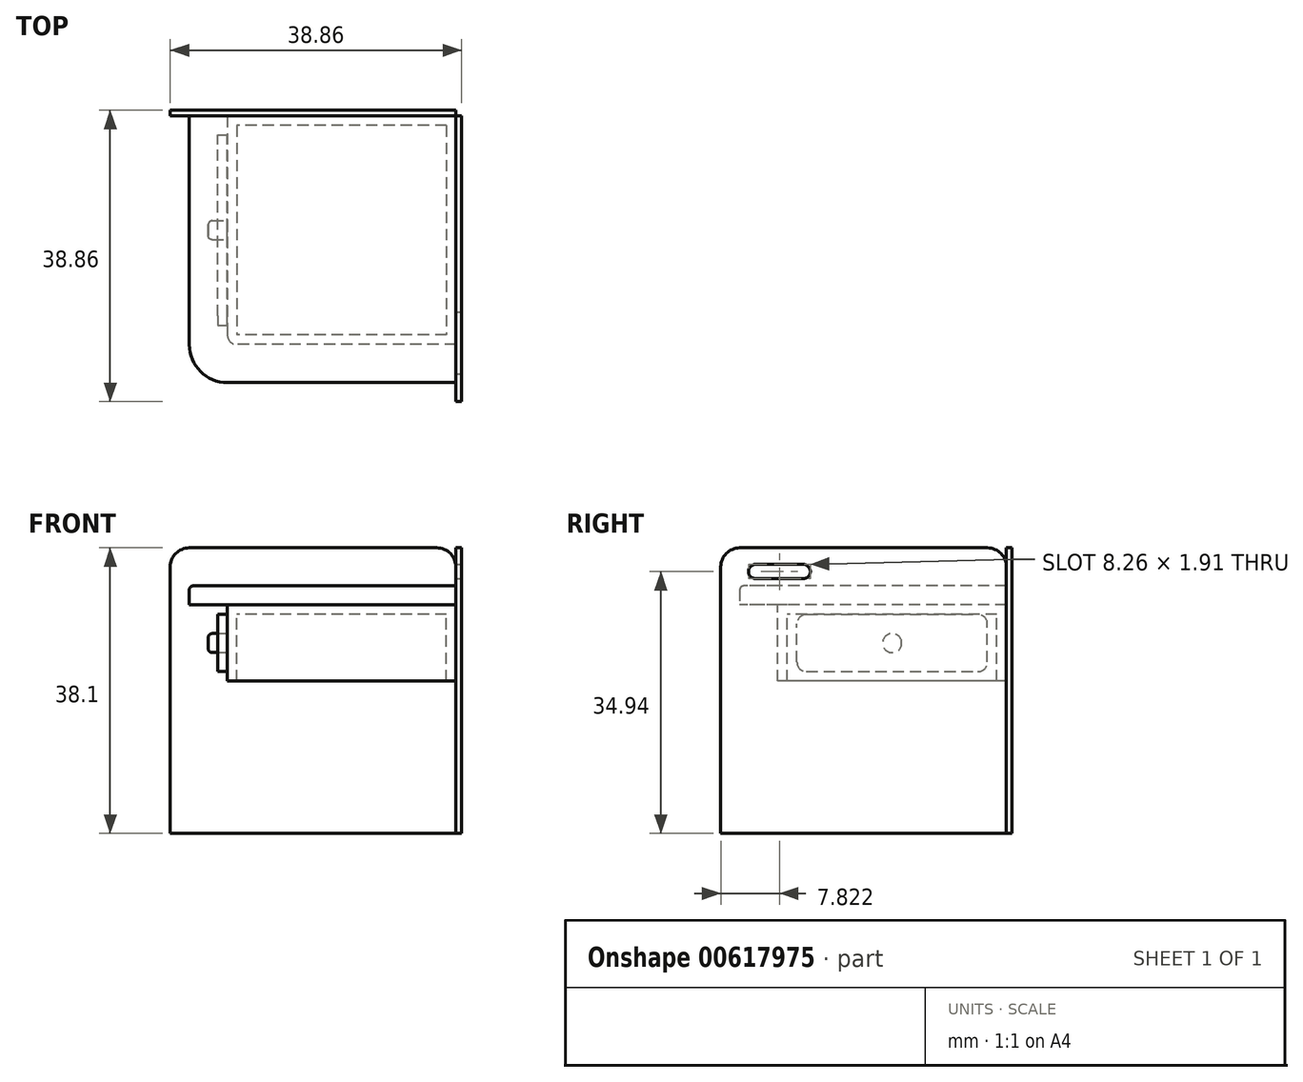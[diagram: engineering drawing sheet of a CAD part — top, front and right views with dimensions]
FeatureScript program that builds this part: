
annotation { "Feature Type Name" : "Feature", "Feature Type Description" : "" }
export const myFeature = defineFeature(function(context is Context, id is Id, definition is map)
    precondition{}
    {
        {
            var Q0;
            Q0=qCreatedBy(makeId("Right.planeOp"),FACE);
            var sketch = newSketch(context, id + "F0", { "sketchPlane" : qUnion([Q0])});
            skLineSegment(sketch, "E0.bottom", {"start": v(0, 0) * mm, "end": v(-38.1, 0) * mm});
            skLineSegment(sketch, "E0.top", {"start": v(0, 38.1) * mm, "end": v(-38.1, 38.1) * mm});
            skLineSegment(sketch, "E0.left", {"start": v(0, 0) * mm, "end": v(0, 38.1) * mm});
            skLineSegment(sketch, "E0.right", {"start": v(-38.1, 0) * mm, "end": v(-38.1, 38.1) * mm});
            skSolve(sketch);
        }
        {
            var Q0;
            Q0=qCreatedBy(makeId("Front.planeOp"),FACE);
            var sketch = newSketch(context, id + "F1", { "sketchPlane" : qUnion([Q0])});
            skLineSegment(sketch, "E1.0", {"start": v(0, 0) * mm, "end": v(0, 38.1) * mm});
            skLineSegment(sketch, "E2.bottom", {"start": v(0, 38.1) * mm, "end": v(38.1, 38.1) * mm});
            skLineSegment(sketch, "E2.top", {"start": v(0, 0) * mm, "end": v(38.1, 0) * mm});
            skLineSegment(sketch, "E2.left", {"start": v(0, 38.1) * mm, "end": v(0, 0) * mm});
            skLineSegment(sketch, "E2.right", {"start": v(38.1, 38.1) * mm, "end": v(38.1, 0) * mm});
            skLineSegment(sketch, "E3.bottom", {"start": v(38.1, 38.1) * mm, "end": v(76.2, 38.1) * mm});
            skLineSegment(sketch, "E3.top", {"start": v(38.1, 0) * mm, "end": v(76.2, 0) * mm});
            skLineSegment(sketch, "E3.right", {"start": v(76.2, 38.1) * mm, "end": v(76.2, 0) * mm});
            skSolve(sketch);
        }
        {
            var Q0;
            Q0=makeQuery(id+"F0.imprint","IMPRINT",FACE,{"disambiguationData":[TD([[makeQuery(id+"F0.imprint","IMPRINT",EDGE,{"derivedFrom":sQuery(id+"F0.wireOp",EDGE,"E0.bottom")}),-1.0]])]});
            extrude(context, id + "F2", {"entities" : qUnion([Q0]), "oppositeDirection" : true, "depth" : 0.76 * mm, "offsetDistance" : 25.4 * mm});
        }
        {
            var Q0;
            Q0=makeQuery(id+"F1.imprint","IMPRINT",FACE,{"disambiguationData":[TD([[makeQuery(id+"F1.imprint","IMPRINT",EDGE,{"derivedFrom":sQuery(id+"F1.wireOp",EDGE,"E2.bottom")}),-1.0]])]});
            extrude(context, id + "F3", {"entities" : qUnion([Q0]), "depth" : 0.76 * mm, "offsetDistance" : 25.4 * mm});
        }
        {
            var Q0;
            Q0=qCreatedBy(makeId("Top.planeOp"),FACE);
            var sketch = newSketch(context, id + "F4", { "sketchPlane" : qUnion([Q0])});
            skPoint(sketch, "E4.0", {"position": v(0, -0.8) * mm});
            skLineSegment(sketch, "E5.bottom", {"start": v(0, -0.8) * mm, "end": v(35.56, -0.8) * mm});
            skLineSegment(sketch, "E5.top", {"start": v(0, -36.36) * mm, "end": v(35.56, -36.36) * mm});
            skLineSegment(sketch, "E5.left", {"start": v(0, -0.8) * mm, "end": v(0, -36.36) * mm});
            skLineSegment(sketch, "E5.right", {"start": v(35.56, -0.8) * mm, "end": v(35.56, -36.36) * mm});
            skSolve(sketch);
        }
        {
            var Q0;
            Q0=makeQuery(id+"F4.imprint","IMPRINT",FACE,{"disambiguationData":[TD([[makeQuery(id+"F4.imprint","IMPRINT",EDGE,{"derivedFrom":sQuery(id+"F4.wireOp",EDGE,"E5.bottom")}),-1.0]])]});
            extrude(context, id + "F5", {"entities" : qUnion([Q0]), "depth" : 17.78 * mm});
        }
        {
            var Q0;
            Q0=makeQuery(id+"F5.opExtrude","CAP_FACE",FACE,{"disambiguationData":[OSD([sQuery(id+"F4.wireOp",EDGE,"E5.bottom"),sQuery(id+"F4.wireOp",EDGE,"E5.top"),sQuery(id+"F4.wireOp",EDGE,"E5.left"),sQuery(id+"F4.wireOp",EDGE,"E5.right")])],"isStart":false});
            cPlane(context, id + "F6", {"entities" : qUnion([Q0]), "cplaneType" : CPlaneType.OFFSET, "offset" : 12.7 * mm, "width" : 152.4 * mm, "height" : 152.4 * mm});
        }
        {
            var Q0;
            Q0=qCreatedBy(id+"F6.planeOp",FACE);
            var sketch = newSketch(context, id + "F7", { "sketchPlane" : qUnion([Q0])});
            skLineSegment(sketch, "E6.bottom", {"start": v(76.2, -0.76) * mm, "end": v(40.64, -0.76) * mm});
            skLineSegment(sketch, "E6.top", {"start": v(76.2, -36.32) * mm, "end": v(40.64, -36.32) * mm});
            skLineSegment(sketch, "E6.left", {"start": v(76.2, -0.76) * mm, "end": v(76.2, -36.32) * mm});
            skLineSegment(sketch, "E6.right", {"start": v(40.64, -0.76) * mm, "end": v(40.64, -36.32) * mm});
            skSolve(sketch);
        }
        {
            var Q0;
            Q0=qCreatedBy(id+"F6.planeOp",FACE);
            var sketch = newSketch(context, id + "F8", { "sketchPlane" : qUnion([Q0])});
            skLineSegment(sketch, "E7.bottom", {"start": v(76.2, -0.76) * mm, "end": v(45.72, -0.76) * mm});
            skLineSegment(sketch, "E7.top", {"start": v(76.2, -31.24) * mm, "end": v(45.72, -31.24) * mm});
            skLineSegment(sketch, "E7.left", {"start": v(76.2, -0.76) * mm, "end": v(76.2, -31.24) * mm});
            skLineSegment(sketch, "E7.right", {"start": v(45.72, -0.76) * mm, "end": v(45.72, -31.24) * mm});
            skSolve(sketch);
        }
        {
            var Q0;
            Q0=makeQuery(id+"F8.imprint","IMPRINT",FACE,{"disambiguationData":[TD([[makeQuery(id+"F8.imprint","IMPRINT",EDGE,{"derivedFrom":sQuery(id+"F8.wireOp",EDGE,"E7.bottom")}),1.0]])]});
            extrude(context, id + "F9", {"entities" : qUnion([Q0]), "oppositeDirection" : true, "depth" : 10.16 * mm});
        }
        {
            var Q0;
            Q0=qSketchRegion(id+"F7",true);
            extrude(context, id + "F10", {"entities" : qUnion([Q0]), "depth" : 2.54 * mm});
        }
        {
            var Q0;
            Q0=makeQuery(id+"F5.opExtrude","SWEPT_FACE",FACE,{"disambiguationData":[OSD([sQuery(id+"F4.wireOp",EDGE,"E5.top")])]});
            var sketch = newSketch(context, id + "F11", { "sketchPlane" : qUnion([Q0])});
            skLineSegment(sketch, "E8.0", {"start": v(35.56, 17.78) * mm, "end": v(35.56, 0) * mm});
            skLineSegment(sketch, "E9.0.2", {"start": v(35.56, 17.78) * mm, "end": v(0, 17.78) * mm});
            skLineSegment(sketch, "E9.0.3", {"start": v(0, 17.78) * mm, "end": v(0, 0) * mm});
            skLineSegment(sketch, "E10.bottom", {"start": v(33.78, 15.24) * mm, "end": v(3.3, 15.24) * mm});
            skLineSegment(sketch, "E10.top", {"start": v(33.78, 2.54) * mm, "end": v(3.3, 2.54) * mm});
            skLineSegment(sketch, "E10.left", {"start": v(33.78, 15.24) * mm, "end": v(33.78, 2.54) * mm});
            skLineSegment(sketch, "E10.right", {"start": v(3.3, 15.24) * mm, "end": v(3.3, 2.54) * mm});
            skPoint(sketch, "E10.middle", {"position": v(18.54, 8.9) * mm});
            skSolve(sketch);
        }
        {
            var Q0;
            Q0=makeQuery(id+"F11.imprint","IMPRINT",FACE,{"disambiguationData":[TD([[makeQuery(id+"F11.imprint","IMPRINT",EDGE,{"derivedFrom":sQuery(id+"F11.wireOp",EDGE,"E10.bottom")}),1.0]])]});
            extrude(context, id + "F12", {"entities" : qUnion([Q0]), "depth" : 1.27 * mm});
        }
        {
            var Q0;
            Q0=makeQuery(id+"F12.opExtrude","CAP_FACE",FACE,{"disambiguationData":[OSD([sQuery(id+"F11.wireOp",EDGE,"E10.bottom"),sQuery(id+"F11.wireOp",EDGE,"E10.top"),sQuery(id+"F11.wireOp",EDGE,"E10.left"),sQuery(id+"F11.wireOp",EDGE,"E10.right")])],"isStart":false});
            var sketch = newSketch(context, id + "F13", { "sketchPlane" : qUnion([Q0])});
            skCircle(sketch, "E11", {"center": v(18.54, 8.89) * mm, "radius": 1.27 * mm});
            skSolve(sketch);
        }
        {
            var Q0;
            Q0=makeQuery(id+"F13.imprint","IMPRINT",FACE,{"disambiguationData":[TD([[makeQuery(id+"F13.imprint","IMPRINT",EDGE,{"derivedFrom":sQuery(id+"F13.wireOp",EDGE,"E11")}),1.0]])]});
            extrude(context, id + "F14", {"entities" : qUnion([Q0]), "depth" : 1.27 * mm});
        }
        {
            var Q0;
            Q0=makeQuery(id+"F9.opExtrude","SWEPT_FACE",FACE,{"disambiguationData":[OSD([sQuery(id+"F8.wireOp",EDGE,"E7.right")])]});
            var sketch = newSketch(context, id + "F15", { "sketchPlane" : qUnion([Q0])});
            skLineSegment(sketch, "E12.bottom", {"start": v(28.7, 21.59) * mm, "end": v(3.3, 21.59) * mm});
            skLineSegment(sketch, "E12.top", {"start": v(28.7, 29.2) * mm, "end": v(3.3, 29.2) * mm});
            skLineSegment(sketch, "E12.left", {"start": v(28.7, 21.59) * mm, "end": v(28.7, 29.2) * mm});
            skLineSegment(sketch, "E12.right", {"start": v(3.3, 21.59) * mm, "end": v(3.3, 29.2) * mm});
            skPoint(sketch, "E12.middle", {"position": v(16, 25.4) * mm});
            skSolve(sketch);
        }
        {
            var Q0;
            Q0=makeQuery(id+"F15.imprint","IMPRINT",FACE,{"disambiguationData":[TD([[makeQuery(id+"F15.imprint","IMPRINT",EDGE,{"derivedFrom":sQuery(id+"F15.wireOp",EDGE,"E12.bottom")}),1.0]])]});
            var sketch = newSketch(context, id + "F16", { "sketchPlane" : qUnion([Q0])});
            skCircle(sketch, "E13", {"center": v(16, 25.4) * mm, "radius": 1.27 * mm});
            skSolve(sketch);
        }
        {
            var Q0;
            Q0=makeQuery(id+"F16.imprint","IMPRINT",FACE,{"disambiguationData":[TD([[makeQuery(id+"F16.imprint","IMPRINT",EDGE,{"derivedFrom":sQuery(id+"F16.wireOp",EDGE,"E13")}),1.0]])]});
            extrude(context, id + "F17", {"entities" : qUnion([Q0]), "depth" : 2.54 * mm});
        }
        {
            var Q0;
            Q0=makeQuery(id+"F15.imprint","IMPRINT",FACE,{"disambiguationData":[TD([[makeQuery(id+"F15.imprint","IMPRINT",EDGE,{"derivedFrom":sQuery(id+"F15.wireOp",EDGE,"E12.bottom")}),-1.0]])]});
            extrude(context, id + "F18", {"entities" : qUnion([Q0]), "depth" : 1.27 * mm});
        }
        {
            var Q0;
            Q0=makeQuery(id+"F2.opExtrude","SWEPT_EDGE",EDGE,{"disambiguationData":[OSD([sQuery(id+"F0.wireOp",EDGE,"E0.top"),sQuery(id+"F0.wireOp",EDGE,"E0.right")])]});
            var Q1;
            Q1=makeQuery(id+"F2.opExtrude","SWEPT_EDGE",EDGE,{"disambiguationData":[OSD([sQuery(id+"F0.wireOp",EDGE,"E0.top"),sQuery(id+"F0.wireOp",EDGE,"E0.left")])]});
            var Q2;
            Q2=makeQuery(id+"F3.opExtrude","SWEPT_EDGE",EDGE,{"disambiguationData":[OSD([sQuery(id+"FI0QwBpxzJms6q6_1.wireOp",EDGE,"EPlBsMqQ-QzQ8-VdCQ-xvKd-hzmvY7jMW2L1.bottom"),sQuery(id+"FI0QwBpxzJms6q6_1.wireOp",EDGE,"EPlBsMqQ-QzQ8-VdCQ-xvKd-hzmvY7jMW2L1.right")])]});
            var Q3;
            Q3=makeQuery(id+"FcK2yJQiMoCniT7_2.opExtrude","SWEPT_EDGE",EDGE,{"disambiguationData":[OSD([sQuery(id+"FKOlXeHhfTV6Gp4_1.wireOp",EDGE,"gBm9quYi-xdeT-jJYe-hTa2-NPwO5Kq9pGmv.bottom"),sQuery(id+"FKOlXeHhfTV6Gp4_1.wireOp",EDGE,"gBm9quYi-xdeT-jJYe-hTa2-NPwO5Kq9pGmv.right")])]});
            var Q4;
            Q4=makeQuery(id+"FcK2yJQiMoCniT7_2.opExtrude","SWEPT_EDGE",EDGE,{"disambiguationData":[OSD([sQuery(id+"FKOlXeHhfTV6Gp4_1.wireOp",EDGE,"gBm9quYi-xdeT-jJYe-hTa2-NPwO5Kq9pGmv.bottom"),sQuery(id+"FKOlXeHhfTV6Gp4_1.wireOp",EDGE,"gBm9quYi-xdeT-jJYe-hTa2-NPwO5Kq9pGmv.left")])]});
            var Q5;
            Q5=makeQuery(id+"F3.opExtrude","SWEPT_EDGE",EDGE,{"disambiguationData":[OSD([sQuery(id+"F1.wireOp",EDGE,"E3.bottom"),sQuery(id+"F1.wireOp",EDGE,"E3.right")])]});
            var Q6;
            Q6=makeQuery(id+"F3.opExtrude","SWEPT_EDGE",EDGE,{"disambiguationData":[OSD([sQuery(id+"F1.wireOp",EDGE,"E2.bottom"),sQuery(id+"F1.wireOp",EDGE,"E2.left")])]});
            fillet(context, id + "F19", {"entities" : qUnion([Q0, Q1, Q2, Q3, Q4, Q5, Q6]), "radius" : 2.54 * mm, "tangentPropagation" : true, "allowEdgeOverflow" : false});
        }
        {
            var Q0;
            Q0=makeQuery(id+"F10.opExtrude","SWEPT_EDGE",EDGE,{"disambiguationData":[OSD([sQuery(id+"F7.wireOp",EDGE,"E6.top"),sQuery(id+"F7.wireOp",EDGE,"E6.right")])]});
            fillet(context, id + "F20", {"entities" : qUnion([Q0]), "radius" : 5.08 * mm, "tangentPropagation" : true, "allowEdgeOverflow" : false});
        }
        {
            var Q0;
            Q0=makeQuery(id+"F9.opExtrude","SWEPT_EDGE",EDGE,{"disambiguationData":[OSD([sQuery(id+"F8.wireOp",EDGE,"E7.top"),sQuery(id+"F8.wireOp",EDGE,"E7.right")])]});
            var Q1;
            Q1=makeQuery(id+"F5.opExtrude","CAP_EDGE",EDGE,{"disambiguationData":[OSD([sQuery(id+"F4.wireOp",EDGE,"E5.right")])],"isStart":false});
            fillet(context, id + "F21", {"entities" : qUnion([Q0, Q1]), "radius" : 1.27 * mm, "tangentPropagation" : true, "allowEdgeOverflow" : false});
        }
        {
            var Q0;
            Q0=makeQuery(id+"F2.opExtrude","CAP_FACE",FACE,{"disambiguationData":[OSD([sQuery(id+"F0.wireOp",EDGE,"E0.bottom"),sQuery(id+"F0.wireOp",EDGE,"E0.top"),sQuery(id+"F0.wireOp",EDGE,"E0.left"),sQuery(id+"F0.wireOp",EDGE,"E0.right")])],"isStart":true});
            var sketch = newSketch(context, id + "F22", { "sketchPlane" : qUnion([Q0])});
            skLineSegment(sketch, "E14.left", {"start": v(33.38, 34.48) * mm, "end": v(33.38, 28.13) * mm});
            skLineSegment(sketch, "E14.right", {"start": v(35.28, 34.48) * mm, "end": v(35.28, 28.13) * mm});
            skArc(sketch, "E15", {"start": v(35.28, 34.48) * mm, "mid": v(34.33, 35.43) * mm, "end": v(33.38, 34.48) * mm});
            skArc(sketch, "E16", {"start": v(33.38, 28.13) * mm, "mid": v(34.33, 27.18) * mm, "end": v(35.28, 28.13) * mm});
            skSolve(sketch);
        }
        {
            var Q0;
            Q0=qSketchRegion(id+"F22",true);
            extrude(context, id + "F23", {"entities" : qUnion([Q0]), "operationType" : NewBodyOperationType.REMOVE, "oppositeDirection" : true, "depth" : 12.7 * mm, "offsetDistance" : 25.4 * mm});
        }
        {
            var Q0;
            Q0=makeQuery(id+"F1.imprint","IMPRINT",FACE,{"disambiguationData":[TD([[makeQuery(id+"F1.imprint","IMPRINT",EDGE,{"derivedFrom":sQuery(id+"F1.wireOp",EDGE,"E3.bottom")}),-1.0]])]});
            extrude(context, id + "F24", {"entities" : qUnion([Q0]), "depth" : 0.76 * mm, "offsetDistance" : 25.4 * mm});
        }
        {
            var Q0;
            Q0=qCreatedBy(makeId("Right.planeOp"),FACE);
            cPlane(context, id + "F25", {"entities" : qUnion([Q0]), "cplaneType" : CPlaneType.OFFSET, "offset" : 76.2 * mm, "width" : 152.4 * mm, "height" : 152.4 * mm});
        }
        {
            var Q0;
            Q0=qCreatedBy(id+"F25.planeOp",FACE);
            var sketch = newSketch(context, id + "F26", { "sketchPlane" : qUnion([Q0])});
            skLineSegment(sketch, "E17.bottom", {"start": v(-0.76, 38.1) * mm, "end": v(-38.86, 38.1) * mm});
            skLineSegment(sketch, "E17.top", {"start": v(-0.76, 0) * mm, "end": v(-38.86, 0) * mm});
            skLineSegment(sketch, "E17.left", {"start": v(-0.76, 38.1) * mm, "end": v(-0.76, 0) * mm});
            skLineSegment(sketch, "E17.right", {"start": v(-38.86, 38.1) * mm, "end": v(-38.86, 0) * mm});
            skSolve(sketch);
        }
        {
            var Q0;
            Q0=qSketchRegion(id+"F26",true);
            extrude(context, id + "F27", {"entities" : qUnion([Q0]), "depth" : 0.76 * mm, "offsetDistance" : 25.4 * mm});
        }
        {
            var Q0;
            Q0=makeQuery(id+"F27.opExtrude","CAP_FACE",FACE,{"disambiguationData":[OSD([sQuery(id+"F26.wireOp",EDGE,"E17.bottom"),sQuery(id+"F26.wireOp",EDGE,"E17.top"),sQuery(id+"F26.wireOp",EDGE,"E17.left"),sQuery(id+"F26.wireOp",EDGE,"E17.right")])],"isStart":false});
            var sketch = newSketch(context, id + "F28", { "sketchPlane" : qUnion([Q0])});
            skLineSegment(sketch, "E18.bottom", {"start": v(-34.21, 35.9) * mm, "end": v(-27.86, 35.9) * mm});
            skLineSegment(sketch, "E18.top", {"start": v(-34.21, 33.99) * mm, "end": v(-27.86, 33.99) * mm});
            skArc(sketch, "E19", {"start": v(-27.86, 33.99) * mm, "mid": v(-26.91, 34.94) * mm, "end": v(-27.86, 35.9) * mm});
            skArc(sketch, "E20", {"start": v(-34.21, 35.9) * mm, "mid": v(-35.17, 34.94) * mm, "end": v(-34.21, 33.99) * mm});
            skSolve(sketch);
        }
        {
            var Q0;
            Q0=makeQuery(id+"F28.imprint","IMPRINT",FACE,{"disambiguationData":[TD([[makeQuery(id+"F28.imprint","IMPRINT",EDGE,{"derivedFrom":sQuery(id+"F28.wireOp",EDGE,"E18.bottom")}),-1.0]])]});
            extrude(context, id + "F29", {"entities" : qUnion([Q0]), "operationType" : NewBodyOperationType.REMOVE, "oppositeDirection" : true, "depth" : 12.7 * mm, "offsetDistance" : 25.4 * mm});
        }
        {
            var Q0;
            Q0=makeQuery(id+"F24.opExtrude","SWEPT_EDGE",EDGE,{"disambiguationData":[OSD([sQuery(id+"F1.wireOp",EDGE,"E3.bottom"),sQuery(id+"F1.wireOp",EDGE,"E3.right")])]});
            var Q1;
            Q1=makeQuery(id+"F27.opExtrude","SWEPT_EDGE",EDGE,{"disambiguationData":[OSD([sQuery(id+"F26.wireOp",EDGE,"E17.bottom"),sQuery(id+"F26.wireOp",EDGE,"E17.left")])]});
            var Q2;
            Q2=makeQuery(id+"F24.opExtrude","SWEPT_EDGE",EDGE,{"disambiguationData":[OSD([sQuery(id+"F1.wireOp",EDGE,"E2.bottom"),sQuery(id+"F1.wireOp",EDGE,"E3.bottom"),sQuery(id+"F1.wireOp",EDGE,"E2.right")])]});
            var Q3;
            Q3=makeQuery(id+"F27.opExtrude","SWEPT_EDGE",EDGE,{"disambiguationData":[OSD([sQuery(id+"F26.wireOp",EDGE,"E17.bottom"),sQuery(id+"F26.wireOp",EDGE,"E17.right")])]});
            fillet(context, id + "F30", {"entities" : qUnion([Q0, Q1, Q2, Q3]), "radius" : 2.54 * mm, "tangentPropagation" : true, "allowEdgeOverflow" : false});
        }
        {
            var Q0;
            Q0=makeQuery(id+"F9.opExtrude","CAP_FACE",FACE,{"disambiguationData":[OSD([sQuery(id+"F8.wireOp",EDGE,"E7.bottom"),sQuery(id+"F8.wireOp",EDGE,"E7.top"),sQuery(id+"F8.wireOp",EDGE,"E7.left"),sQuery(id+"F8.wireOp",EDGE,"E7.right")])],"isStart":false});
            shell(context, id + "F31", {"entities" : qUnion([Q0]), "thickness" : 1.27 * mm});
        }
        {
            var Q0;
            Q0=makeQuery(id+"F2.opExtrude","CAP_FACE",FACE,{"disambiguationData":[OSD([sQuery(id+"F0.wireOp",EDGE,"E0.bottom"),sQuery(id+"F0.wireOp",EDGE,"E0.top"),sQuery(id+"F0.wireOp",EDGE,"E0.left"),sQuery(id+"F0.wireOp",EDGE,"E0.right")])],"isStart":false});
            var sketch = newSketch(context, id + "F32", { "sketchPlane" : qUnion([Q0])});
            skLineSegment(sketch, "E21.left", {"start": v(33.37, 33.56) * mm, "end": v(33.37, 27.2) * mm});
            skLineSegment(sketch, "E21.right", {"start": v(35.27, 33.56) * mm, "end": v(35.27, 27.2) * mm});
            skArc(sketch, "E22", {"start": v(35.27, 33.56) * mm, "mid": v(34.32, 34.5) * mm, "end": v(33.37, 33.56) * mm});
            skArc(sketch, "E23", {"start": v(33.37, 27.2) * mm, "mid": v(34.32, 26.25) * mm, "end": v(35.27, 27.2) * mm});
            skSolve(sketch);
        }
        {
            var Q0;
            Q0=qSketchRegion(id+"F32",true);
            extrude(context, id + "F33", {"entities" : qUnion([Q0]), "operationType" : NewBodyOperationType.REMOVE, "oppositeDirection" : true, "depth" : 25.4 * mm, "offsetDistance" : 25.4 * mm});
        }
        {
            var Q0;
            Q0=makeQuery(id+"F10.opExtrude","CAP_EDGE",EDGE,{"disambiguationData":[OSD([sQuery(id+"F7.wireOp",EDGE,"E6.right")])],"isStart":false});
            fillet(context, id + "F34", {"entities" : qUnion([Q0]), "radius" : 0.5 * mm, "tangentPropagation" : true, "allowEdgeOverflow" : false});
        }
        {
            var Q0;
            Q0=makeQuery(id+"F14.opExtrude","CAP_FACE",FACE,{"disambiguationData":[OSD([sQuery(id+"F13.wireOp",EDGE,"E11")])],"isStart":false});
            fillet(context, id + "F35", {"entities" : qUnion([Q0]), "radius" : 0.5 * mm, "tangentPropagation" : true, "allowEdgeOverflow" : false});
        }
        {
            var Q0;
            Q0=makeQuery(id+"F17.opExtrude","CAP_EDGE",EDGE,{"disambiguationData":[OSD([sQuery(id+"F16.wireOp",EDGE,"E13")])],"isStart":false});
            fillet(context, id + "F36", {"entities" : qUnion([Q0]), "radius" : 0.5 * mm, "tangentPropagation" : true, "allowEdgeOverflow" : false});
        }
        {
            var Q0;
            Q0=makeQuery(id+"F12.opExtrude","SWEPT_EDGE",EDGE,{"disambiguationData":[OSD([sQuery(id+"F11.wireOp",EDGE,"E10.bottom"),sQuery(id+"F11.wireOp",EDGE,"E10.right")])]});
            var Q1;
            Q1=makeQuery(id+"F12.opExtrude","SWEPT_EDGE",EDGE,{"disambiguationData":[OSD([sQuery(id+"F11.wireOp",EDGE,"E10.top"),sQuery(id+"F11.wireOp",EDGE,"E10.right")])]});
            var Q2;
            Q2=makeQuery(id+"F12.opExtrude","SWEPT_EDGE",EDGE,{"disambiguationData":[OSD([sQuery(id+"F11.wireOp",EDGE,"E10.top"),sQuery(id+"F11.wireOp",EDGE,"E10.left")])]});
            var Q3;
            Q3=makeQuery(id+"F12.opExtrude","SWEPT_EDGE",EDGE,{"disambiguationData":[OSD([sQuery(id+"F11.wireOp",EDGE,"E10.bottom"),sQuery(id+"F11.wireOp",EDGE,"E10.left")])]});
            fillet(context, id + "F37", {"entities" : qUnion([Q0, Q1, Q2, Q3]), "radius" : 2.54 * mm, "tangentPropagation" : true, "allowEdgeOverflow" : false});
        }
        {
            var Q0;
            Q0=makeQuery(id+"F18.opExtrude","SWEPT_EDGE",EDGE,{"disambiguationData":[OSD([sQuery(id+"F15.wireOp",EDGE,"E12.bottom"),sQuery(id+"F15.wireOp",EDGE,"E12.left")])]});
            var Q1;
            Q1=makeQuery(id+"F18.opExtrude","SWEPT_EDGE",EDGE,{"disambiguationData":[OSD([sQuery(id+"F15.wireOp",EDGE,"E12.top"),sQuery(id+"F15.wireOp",EDGE,"E12.left")])]});
            var Q2;
            Q2=makeQuery(id+"F18.opExtrude","SWEPT_EDGE",EDGE,{"disambiguationData":[OSD([sQuery(id+"F15.wireOp",EDGE,"E12.bottom"),sQuery(id+"F15.wireOp",EDGE,"E12.right")])]});
            var Q3;
            Q3=makeQuery(id+"F18.opExtrude","SWEPT_EDGE",EDGE,{"disambiguationData":[OSD([sQuery(id+"F15.wireOp",EDGE,"E12.top"),sQuery(id+"F15.wireOp",EDGE,"E12.right")])]});
            fillet(context, id + "F38", {"entities" : qUnion([Q0, Q1, Q2, Q3]), "radius" : 1.27 * mm, "tangentPropagation" : true, "allowEdgeOverflow" : false});
        }
        {
            var Q0;
            Q0=makeQuery(id+"F14.opExtrude","SWEPT_BODY",BODY,{"disambiguationData":[OSD([sQuery(id+"F13.wireOp",EDGE,"E11")])]});
            var Q1;
            Q1=makeQuery(id+"F12.opExtrude","SWEPT_BODY",BODY,{"disambiguationData":[OSD([sQuery(id+"F11.wireOp",EDGE,"E10.bottom"),sQuery(id+"F11.wireOp",EDGE,"E10.top"),sQuery(id+"F11.wireOp",EDGE,"E10.left"),sQuery(id+"F11.wireOp",EDGE,"E10.right")])]});
            var Q2;
            Q2=makeQuery(id+"F5.opExtrude","SWEPT_BODY",BODY,{"disambiguationData":[OSD([sQuery(id+"F4.wireOp",EDGE,"E5.bottom"),sQuery(id+"F4.wireOp",EDGE,"E5.top"),sQuery(id+"F4.wireOp",EDGE,"E5.left"),sQuery(id+"F4.wireOp",EDGE,"E5.right")])]});
            var Q3;
            Q3=makeQuery(id+"F3.opExtrude","SWEPT_BODY",BODY,{"disambiguationData":[OSD([sQuery(id+"F1.wireOp",EDGE,"E2.bottom"),sQuery(id+"F1.wireOp",EDGE,"E2.top"),sQuery(id+"F1.wireOp",EDGE,"E2.left"),sQuery(id+"F1.wireOp",EDGE,"E2.right")])]});
            var Q4;
            Q4=makeQuery(id+"F2.opExtrude","SWEPT_BODY",BODY,{"disambiguationData":[OSD([sQuery(id+"F0.wireOp",EDGE,"E0.bottom"),sQuery(id+"F0.wireOp",EDGE,"E0.top"),sQuery(id+"F0.wireOp",EDGE,"E0.left"),sQuery(id+"F0.wireOp",EDGE,"E0.right")])]});
            deleteBodies(context, id + "F39", {"entities" : qUnion([Q0, Q1, Q2, Q3, Q4])});
        }
    });
